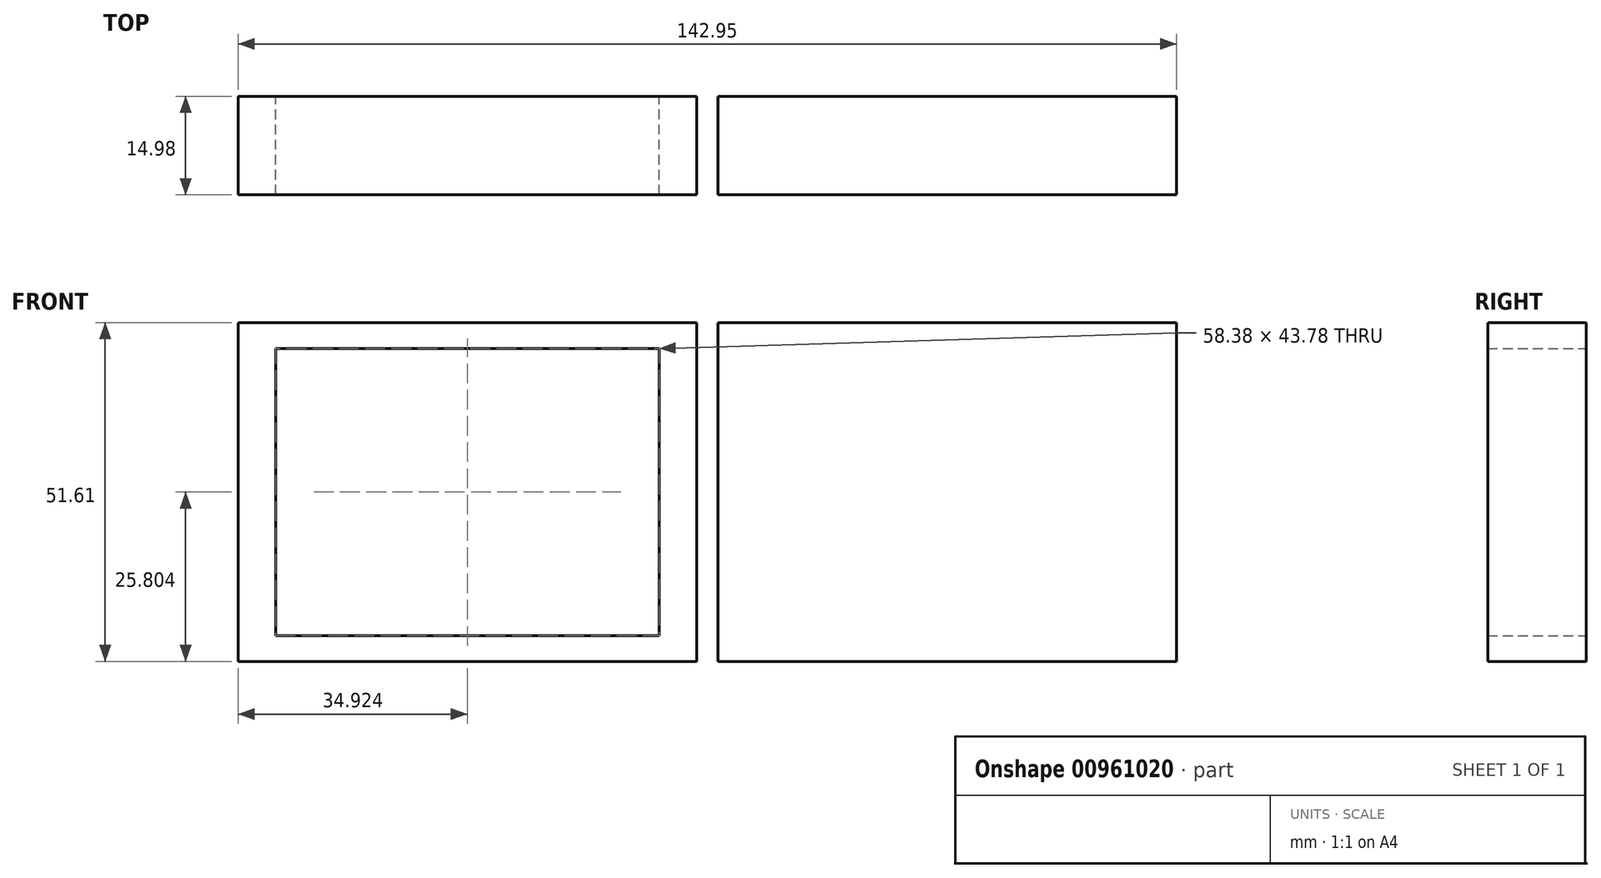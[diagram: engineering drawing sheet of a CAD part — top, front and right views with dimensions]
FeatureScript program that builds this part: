
annotation { "Feature Type Name" : "Feature", "Feature Type Description" : "" }
export const myFeature = defineFeature(function(context is Context, id is Id, definition is map)
    precondition{}
    {
        {
            var Q0;
            Q0=qCreatedBy(makeId("Front.planeOp"),FACE);
            var sketch = newSketch(context, id + "F0", { "sketchPlane" : qUnion([Q0])});
            skLineSegment(sketch, "E0.bottom", {"start": v(-1.3, 15.96) * mm, "end": v(-71.15, 15.96) * mm});
            skLineSegment(sketch, "E0.top", {"start": v(-1.3, 67.57) * mm, "end": v(-71.15, 67.57) * mm});
            skLineSegment(sketch, "E0.left", {"start": v(-1.3, 15.96) * mm, "end": v(-1.3, 67.57) * mm});
            skLineSegment(sketch, "E0.right", {"start": v(-71.15, 15.96) * mm, "end": v(-71.15, 67.57) * mm});
            skPoint(sketch, "E0.middle", {"position": v(-36.23, 41.76) * mm});
            skLineSegment(sketch, "E1.bottom", {"start": v(-65.42, 19.87) * mm, "end": v(-7.04, 19.87) * mm});
            skLineSegment(sketch, "E1.top", {"start": v(-65.42, 63.66) * mm, "end": v(-7.04, 63.66) * mm});
            skLineSegment(sketch, "E1.left", {"start": v(-65.42, 19.87) * mm, "end": v(-65.42, 63.66) * mm});
            skLineSegment(sketch, "E1.right", {"start": v(-7.04, 19.87) * mm, "end": v(-7.04, 63.66) * mm});
            skPoint(sketch, "E2.middle", {"position": v(24.24, -3.32) * mm});
            skLineSegment(sketch, "E3.bottom", {"start": v(71.8, 15.96) * mm, "end": v(1.95, 15.96) * mm});
            skLineSegment(sketch, "E3.top", {"start": v(71.8, 67.57) * mm, "end": v(1.95, 67.57) * mm});
            skLineSegment(sketch, "E3.left", {"start": v(71.8, 15.96) * mm, "end": v(71.8, 67.57) * mm});
            skLineSegment(sketch, "E3.right", {"start": v(1.95, 15.96) * mm, "end": v(1.95, 67.57) * mm});
            skPoint(sketch, "E3.middle", {"position": v(36.88, 41.76) * mm});
            skSolve(sketch);
        }
        {
            var Q0;
            Q0 = qSketchRegion(id + "F0", true);
            extrude(context, id + "F1", {"entities" : qUnion([Q0]), "endBound" : BoundingType.SYMMETRIC, "depth" : 15 * mm, "offsetDistance" : 25.4 * mm});
        }
    });
